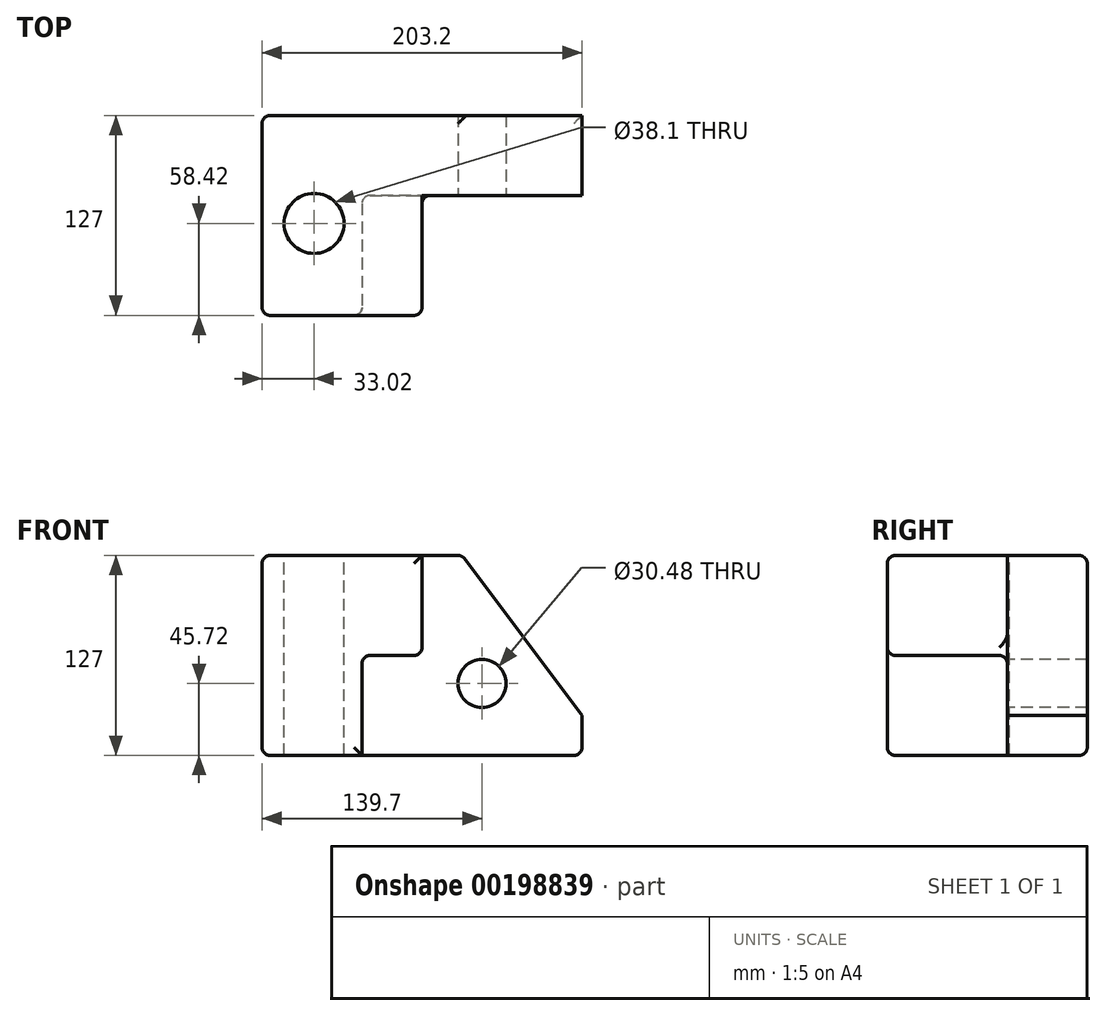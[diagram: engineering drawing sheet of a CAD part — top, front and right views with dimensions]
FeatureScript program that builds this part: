
annotation { "Feature Type Name" : "Feature", "Feature Type Description" : "" }
export const myFeature = defineFeature(function(context is Context, id is Id, definition is map)
    precondition{}
    {
        {
            var Q0;
            Q0=qCreatedBy(makeId("Front.planeOp"),FACE);
            var sketch = newSketch(context, id + "F0", { "sketchPlane" : qUnion([Q0])});
            skLineSegment(sketch, "E0.bottom", {"start": v(101.6, 63.5) * mm, "end": v(-101.6, 63.5) * mm});
            skLineSegment(sketch, "E0.top", {"start": v(101.6, -63.5) * mm, "end": v(-101.6, -63.5) * mm});
            skLineSegment(sketch, "E0.left", {"start": v(101.6, 63.5) * mm, "end": v(101.6, -63.5) * mm});
            skLineSegment(sketch, "E0.right", {"start": v(-101.6, 63.5) * mm, "end": v(-101.6, -63.5) * mm});
            skPoint(sketch, "E0.middle", {"position": v(0, 0) * mm});
            skSolve(sketch);
        }
        {
            var Q0;
            Q0 = qSketchRegion(id + "F0", true);
            extrude(context, id + "F1", {"entities" : qUnion([Q0]), "depth" : 127 * mm});
        }
        {
            var Q0;
            Q0=makeQuery(id+"F1.opExtrude","CAP_FACE",FACE,{"disambiguationData":[OSD([sQuery(id+"F0.wireOp",EDGE,"E0.bottom"),sQuery(id+"F0.wireOp",EDGE,"E0.top"),sQuery(id+"F0.wireOp",EDGE,"E0.left"),sQuery(id+"F0.wireOp",EDGE,"E0.right")])],"isStart":false});
            var sketch = newSketch(context, id + "F2", { "sketchPlane" : qUnion([Q0])});
            skLineSegment(sketch, "E1", {"start": v(-101.6, 63.5) * mm, "end": v(-101.6, -63.5) * mm});
            skLineSegment(sketch, "E2", {"start": v(-38.1, 0) * mm, "end": v(0, 0) * mm});
            skLineSegment(sketch, "E3", {"start": v(0, 0) * mm, "end": v(0, 63.5) * mm});
            skLineSegment(sketch, "E4", {"start": v(0, 63.5) * mm, "end": v(-101.6, 63.5) * mm});
            skLineSegment(sketch, "E5", {"start": v(-38.1, 0) * mm, "end": v(-38.1, -63.5) * mm});
            skLineSegment(sketch, "E6", {"start": v(-38.1, -63.5) * mm, "end": v(-101.6, -63.5) * mm});
            skSolve(sketch);
        }
        {
            var Q0;
            Q0=makeQuery(id+"F2.imprint","IMPRINT",FACE,{"disambiguationData":[TD([[makeQuery(id+"F2.imprint","IMPRINT",EDGE,{"derivedFrom":sQuery(id+"F2.wireOp",EDGE,"E2")}),-1.0]])]});
            extrude(context, id + "F3", {"entities" : qUnion([Q0]), "operationType" : NewBodyOperationType.ADD, "depth" : 25.4 * mm});
        }
        {
            var Q0;
            Q0=makeQuery(id+"F3.opExtrude","CAP_FACE",FACE,{"disambiguationData":[OSD([sQuery(id+"F0.wireOp",EDGE,"E0.bottom"),sQuery(id+"F0.wireOp",EDGE,"E0.top"),sQuery(id+"F0.wireOp",EDGE,"E0.left"),sQuery(id+"F2.wireOp",EDGE,"E2"),sQuery(id+"F2.wireOp",EDGE,"E3"),sQuery(id+"F2.wireOp",EDGE,"E5")])],"isStart":false});
            extrude(context, id + "F4", {"entities" : qUnion([Q0]), "operationType" : NewBodyOperationType.REMOVE, "oppositeDirection" : true, "depth" : 101.6 * mm});
        }
        {
            var Q0;
            {var subQ0=sQuery(id+"F0.wireOp",EDGE,"E0.left");var subQ1=sQuery(id+"F0.wireOp",EDGE,"E0.bottom");Q0=makeQuery(id+"F3.boolean.opBoolean","MERGE",EDGE,{"derivedFrom":[makeQuery(id+"F1.opExtrude","SWEPT_EDGE",EDGE,{"disambiguationData":[OSD([subQ1,subQ0])]}),makeQuery(id+"F3.opExtrude","SWEPT_EDGE",EDGE,{"disambiguationData":[OSD([subQ1,subQ0])]})]});}
            chamfer(context, id + "F5", {"entities" : qUnion([Q0]), "chamferType" : ChamferType.TWO_OFFSETS, "width1" : 76.2 * mm, "oppositeDirection" : false, "width2" : 101.6 * mm, "tangentPropagation" : true});
        }
        {
            var Q0;
            Q0=makeQuery(id+"F1.opExtrude","CAP_EDGE",EDGE,{"disambiguationData":[OSD([sQuery(id+"F0.wireOp",EDGE,"E0.bottom")])],"isStart":false});
            var Q1;
            Q1=makeQuery(id+"F4.boolean.opBoolean","COPY",EDGE,{"derivedFrom":makeQuery(id+"F4.opExtrude","SWEPT_EDGE",EDGE,{"disambiguationData":[OSD([sQuery(id+"F0.wireOp",EDGE,"E0.bottom"),sQuery(id+"F2.wireOp",EDGE,"E3"),sQuery(id+"F2.wireOp",EDGE,"E4")])]})});
            var Q2;
            Q2=makeQuery(id+"F3.opExtrude","CAP_EDGE",EDGE,{"disambiguationData":[OSD([sQuery(id+"F2.wireOp",EDGE,"E3")])],"isStart":true});
            var Q3;
            Q3=makeQuery(id+"F3.opExtrude","CAP_EDGE",EDGE,{"disambiguationData":[OSD([sQuery(id+"F2.wireOp",EDGE,"E2")])],"isStart":true});
            var Q4;
            Q4=makeQuery(id+"F1.opExtrude","CAP_FACE",FACE,{"disambiguationData":[OSD([sQuery(id+"F0.wireOp",EDGE,"E0.bottom"),sQuery(id+"F0.wireOp",EDGE,"E0.top"),sQuery(id+"F0.wireOp",EDGE,"E0.left"),sQuery(id+"F0.wireOp",EDGE,"E0.right")])],"isStart":false});
            var Q5;
            Q5=makeQuery(id+"F4.boolean.opBoolean","COPY",EDGE,{"derivedFrom":makeQuery(id+"F4.opExtrude","SWEPT_EDGE",EDGE,{"disambiguationData":[OSD([sQuery(id+"F0.wireOp",EDGE,"E0.top"),sQuery(id+"F2.wireOp",EDGE,"E5"),sQuery(id+"F2.wireOp",EDGE,"E6")])]})});
            var Q6;
            Q6=makeQuery(id+"F4.boolean.opBoolean","COPY",EDGE,{"derivedFrom":makeQuery(id+"F4.opExtrude","CAP_EDGE",EDGE,{"disambiguationData":[OSD([sQuery(id+"F0.wireOp",EDGE,"E0.top")])],"isStart":false})});
            var Q7;
            Q7=makeQuery(id+"F4.boolean.opBoolean","COPY",EDGE,{"derivedFrom":makeQuery(id+"F4.opExtrude","CAP_EDGE",EDGE,{"disambiguationData":[OSD([sQuery(id+"F2.wireOp",EDGE,"E5")])],"isStart":false})});
            var Q8;
            {var subQ0=sQuery(id+"F0.wireOp",EDGE,"E0.left");var subQ1=sQuery(id+"F0.wireOp",EDGE,"E0.top");Q8=makeQuery(id+"F3.boolean.opBoolean","MERGE",EDGE,{"derivedFrom":[makeQuery(id+"F1.opExtrude","SWEPT_EDGE",EDGE,{"disambiguationData":[OSD([subQ1,subQ0])]}),makeQuery(id+"F3.opExtrude","SWEPT_EDGE",EDGE,{"disambiguationData":[OSD([subQ1,subQ0])]})]});}
            var Q9;
            Q9=makeQuery(id+"F1.opExtrude","CAP_EDGE",EDGE,{"disambiguationData":[OSD([sQuery(id+"F0.wireOp",EDGE,"E0.top")])],"isStart":true});
            var Q10;
            Q10=makeQuery(id+"F1.opExtrude","CAP_EDGE",EDGE,{"disambiguationData":[OSD([sQuery(id+"F0.wireOp",EDGE,"E0.right")])],"isStart":true});
            var Q11;
            Q11=makeQuery(id+"F1.opExtrude","SWEPT_EDGE",EDGE,{"disambiguationData":[OSD([sQuery(id+"F0.wireOp",EDGE,"E0.top"),sQuery(id+"F0.wireOp",EDGE,"E0.right")])]});
            var Q12;
            Q12=makeQuery(id+"F4.boolean.opBoolean","COPY",EDGE,{"derivedFrom":makeQuery(id+"F4.opExtrude","CAP_EDGE",EDGE,{"disambiguationData":[OSD([sQuery(id+"F0.wireOp",EDGE,"E0.bottom")])],"isStart":false})});
            var Q13;
            {var subQ0=sQuery(id+"F0.wireOp",EDGE,"E0.bottom");var subQ1=sQuery(id+"F0.wireOp",EDGE,"E0.left");Q13=makeQuery(id+"F5.opChamfer","BLEND_EDGE",EDGE,{"blendedFrom":[makeQuery(id+"F3.boolean.opBoolean","MERGE",EDGE,{"derivedFrom":[makeQuery(id+"F1.opExtrude","SWEPT_EDGE",EDGE,{"disambiguationData":[OSD([subQ0,subQ1])]}),makeQuery(id+"F3.opExtrude","SWEPT_EDGE",EDGE,{"disambiguationData":[OSD([subQ0,subQ1])]})]}),makeQuery(id+"F3.boolean.opBoolean","MERGE",FACE,{"derivedFrom":[makeQuery(id+"F1.opExtrude","SWEPT_FACE",FACE,{"disambiguationData":[OSD([subQ0])]}),makeQuery(id+"F3.opExtrude","SWEPT_FACE",FACE,{"disambiguationData":[OSD([subQ0])]})]})],"blendedInto":[makeQuery(id+"F3.boolean.opBoolean","MERGE",FACE,{"derivedFrom":[makeQuery(id+"F1.opExtrude","SWEPT_FACE",FACE,{"disambiguationData":[OSD([subQ0])]}),makeQuery(id+"F3.opExtrude","SWEPT_FACE",FACE,{"disambiguationData":[OSD([subQ0])]})]})]});}
            var Q14;
            Q14=makeQuery(id+"F1.opExtrude","CAP_EDGE",EDGE,{"disambiguationData":[OSD([sQuery(id+"F0.wireOp",EDGE,"E0.bottom")])],"isStart":true});
            var Q15;
            Q15=makeQuery(id+"F4.boolean.opBoolean","COPY",EDGE,{"derivedFrom":makeQuery(id+"F4.opExtrude","SWEPT_EDGE",EDGE,{"disambiguationData":[OSD([sQuery(id+"F2.wireOp",EDGE,"E2"),sQuery(id+"F2.wireOp",EDGE,"E3")])]})});
            var Q16;
            Q16=makeQuery(id+"F4.boolean.opBoolean","COPY",EDGE,{"derivedFrom":makeQuery(id+"F4.opExtrude","CAP_EDGE",EDGE,{"disambiguationData":[OSD([sQuery(id+"F2.wireOp",EDGE,"E2")])],"isStart":false})});
            var Q17;
            Q17=makeQuery(id+"F4.boolean.opBoolean","COPY",EDGE,{"derivedFrom":makeQuery(id+"F4.opExtrude","SWEPT_EDGE",EDGE,{"disambiguationData":[OSD([sQuery(id+"F2.wireOp",EDGE,"E2"),sQuery(id+"F2.wireOp",EDGE,"E5")])]})});
            var Q18;
            Q18=makeQuery(id+"F1.opExtrude","SWEPT_EDGE",EDGE,{"disambiguationData":[OSD([sQuery(id+"F0.wireOp",EDGE,"E0.bottom"),sQuery(id+"F0.wireOp",EDGE,"E0.right")])]});
            fillet(context, id + "F6", {"entities" : qUnion([Q0, Q1, Q2, Q3, Q4, Q5, Q6, Q7, Q8, Q9, Q10, Q11, Q12, Q13, Q14, Q15, Q16, Q17, Q18]), "radius" : 5.08 * mm, "tangentPropagation" : true, "allowEdgeOverflow" : false});
        }
        {
            var Q0;
            Q0=makeQuery(id+"F4.boolean.opBoolean","COPY",FACE,{"derivedFrom":makeQuery(id+"F4.opExtrude","CAP_FACE",FACE,{"disambiguationData":[OSD([sQuery(id+"F0.wireOp",EDGE,"E0.bottom"),sQuery(id+"F0.wireOp",EDGE,"E0.top"),sQuery(id+"F0.wireOp",EDGE,"E0.left"),sQuery(id+"F2.wireOp",EDGE,"E2"),sQuery(id+"F2.wireOp",EDGE,"E3"),sQuery(id+"F2.wireOp",EDGE,"E5")])],"isStart":false})});
            var sketch = newSketch(context, id + "F7", { "sketchPlane" : qUnion([Q0])});
            skCircle(sketch, "E7", {"center": v(38.1, -17.78) * mm, "radius": 15.24 * mm});
            skSolve(sketch);
        }
        {
            var Q0;
            Q0=makeQuery(id+"F7.imprint","IMPRINT",FACE,{"disambiguationData":[TD([[makeQuery(id+"F7.imprint","IMPRINT",EDGE,{"derivedFrom":sQuery(id+"F7.wireOp",EDGE,"E7")}),1.0]])]});
            var Q1;
            Q1=makeQuery(id+"F1.opExtrude","CAP_FACE",FACE,{"disambiguationData":[OSD([sQuery(id+"F0.wireOp",EDGE,"E0.bottom"),sQuery(id+"F0.wireOp",EDGE,"E0.top"),sQuery(id+"F0.wireOp",EDGE,"E0.left"),sQuery(id+"F0.wireOp",EDGE,"E0.right")])],"isStart":true});
            extrude(context, id + "F8", {"entities" : qUnion([Q0]), "operationType" : NewBodyOperationType.REMOVE, "endBound" : BoundingType.UP_TO_SURFACE, "oppositeDirection" : true, "endBoundEntityFace" : qUnion([Q1]), "depth" : 25.4 * mm});
        }
        {
            var Q0;
            {var subQ0=sQuery(id+"F0.wireOp",EDGE,"E0.bottom");Q0=makeQuery(id+"F3.boolean.opBoolean","MERGE",FACE,{"derivedFrom":[makeQuery(id+"F1.opExtrude","SWEPT_FACE",FACE,{"disambiguationData":[OSD([subQ0])]}),makeQuery(id+"F3.opExtrude","SWEPT_FACE",FACE,{"disambiguationData":[OSD([subQ0])]})]});}
            var sketch = newSketch(context, id + "F9", { "sketchPlane" : qUnion([Q0])});
            skCircle(sketch, "E8", {"center": v(-68.58, -68.58) * mm, "radius": 19.05 * mm});
            skSolve(sketch);
        }
        {
            var Q0;
            Q0=makeQuery(id+"F9.imprint","IMPRINT",FACE,{"disambiguationData":[TD([[makeQuery(id+"F9.imprint","IMPRINT",EDGE,{"derivedFrom":sQuery(id+"F9.wireOp",EDGE,"E8")}),1.0]])]});
            var Q1;
            {var subQ0=sQuery(id+"F0.wireOp",EDGE,"E0.top");Q1=makeQuery(id+"F3.boolean.opBoolean","MERGE",FACE,{"derivedFrom":[makeQuery(id+"F1.opExtrude","SWEPT_FACE",FACE,{"disambiguationData":[OSD([subQ0])]}),makeQuery(id+"F3.opExtrude","SWEPT_FACE",FACE,{"disambiguationData":[OSD([subQ0])]})]});}
            extrude(context, id + "F10", {"entities" : qUnion([Q0]), "operationType" : NewBodyOperationType.REMOVE, "endBound" : BoundingType.UP_TO_SURFACE, "oppositeDirection" : true, "endBoundEntityFace" : qUnion([Q1]), "depth" : 25.4 * mm});
        }
    });
